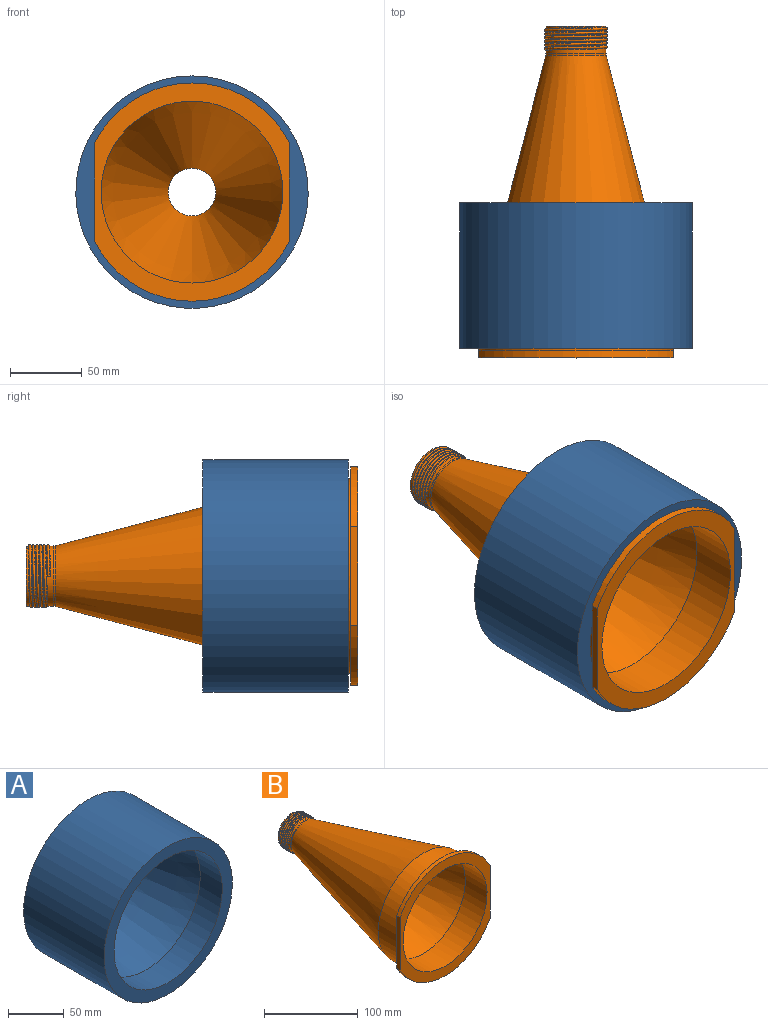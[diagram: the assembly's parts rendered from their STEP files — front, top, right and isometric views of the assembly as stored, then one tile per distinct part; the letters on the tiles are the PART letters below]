
ASSEMBLY  parts=2 mates=1
PART A: 6 faces, bbox 162.3x101.6x162.3 mm
  f0: cylinder r=50.42mm len=100.84mm, axis (0,1,0), area 2333.5mm2, adj f1,f5
  f1: plane 162.26x162.26mm, normal (0,1,0), area 12690.8mm2, adj f0,f2
  f2: cylinder r=81.13mm len=162.26mm, axis (0,1,0), area 51789.6mm2, adj f1,f3
  f3: plane 162.26x162.26mm, normal (0,-1,0), area 5967mm2, adj f2,f4
  f4: cylinder r=68.43mm len=136.86mm, axis (0,1,0), area 12012.6mm2, adj f3,f5
  f5: cone r=68.43mm half-angle=15.2deg, axis (0,-1,0), area 25649mm2, adj f0,f4
PART B: 25 faces, bbox 136.1x231.8x152.6 mm
  f0: plane 135.89x76.2mm, normal (0,1,0), area 1485.1mm2, adj f3,f10,f12,f13
  f1: plane 135.89x76.2mm, normal (0,1,0), area 1485.1mm2, adj f10,f11,f12,f13
  f2: plane 152.4x135.89mm, normal (0,-1,0), area 4805.8mm2, adj f3,f9,f11,f12,f13
  f3: cylinder r=76.2mm len=135.89mm, axis (0,1,0), area 852.4mm2, adj f0,f2,f12,f13
  f4: cone r=21.08mm half-angle=14.7deg, axis (0,-1,0), area 51522.8mm2, adj f7,f10
  f5: cone r=63.5mm half-angle=14.7deg, axis (0,-1,0), area 46384.4mm2, adj f6,f9
  f6: cylinder r=16.65mm len=33.3mm, axis (0,-1,0), area 2141.7mm2, adj f5,f19
  f7: cylinder r=21.08mm len=42.16mm, axis (0,-1,0), area 171.6mm2, adj f4,f8
  f8: plane 42.16x42.16mm, normal (0,1,0), area 20.1mm2, adj f7,f18
  f9: cylinder r=63.5mm len=127mm, axis (0,1,0), area 13174.4mm2, adj f2,f5
  f10: cylinder r=67.95mm len=135.89mm, axis (0,1,0), area 11927.9mm2, adj f0,f1,f4
  f11: cylinder r=76.2mm len=135.89mm, axis (0,1,0), area 852.4mm2, adj f1,f2,f12,f13
  f12: plane 68.99x5.08mm, normal (-1,0,0), area 350.5mm2, adj f0,f1,f2,f3,f11
  f13: plane 68.99x5.08mm, normal (1,0,0), area 350.5mm2, adj f0,f1,f2,f3,f11
  f14: cylinder r=20.93mm len=41.86mm, axis (0,-1,0), area 239.3mm2, adj f15,f19,f20,f23,f24
  f15: cylinder r=20.93mm len=41.86mm, axis (0,-1,0), area 4.4mm2, adj f14,f16,f23,f24
  f16: cylinder r=20.93mm len=41.86mm, axis (0,-1,0), area 4.4mm2, adj f15,f17,f23,f24
  f17: cylinder r=20.93mm len=41.86mm, axis (0,-1,0), area 4.4mm2, adj f16,f18,f23,f24
  f18: cylinder r=20.93mm len=41.86mm, axis (0,-1,0), area 456.4mm2, adj f8,f17,f21,f23,f24
  f19: plane 41.86x41.86mm, normal (0,1,0), area 505.3mm2, adj f6,f14
  f20: plane 2.68x1.22mm, normal (0,0,-1), area 1.5mm2, adj f14,f22,f23,f24
  f21: plane 2.68x1.22mm, normal (0,0,-1), area 1.5mm2, adj f18,f22,f23,f24
  f22: bspline ~52.03x45.06mm, area 1671.7mm2, adj f20,f21,f23,f24
  f23: bspline ~42.63x42.63mm, area 486.2mm2, adj f14,f15,f16,f17,f18,f20,f21,f22
  f24: bspline ~42.63x42.63mm, area 486.1mm2, adj f14,f15,f16,f17,f18,f20,f21,f22
PLACE A t=(0,-103.01,0)mm
PLACE B at identity fixed
MATE slider B.f10 <-> A.f0  axis (0,1,0) through (0,-192.13,0)mm
